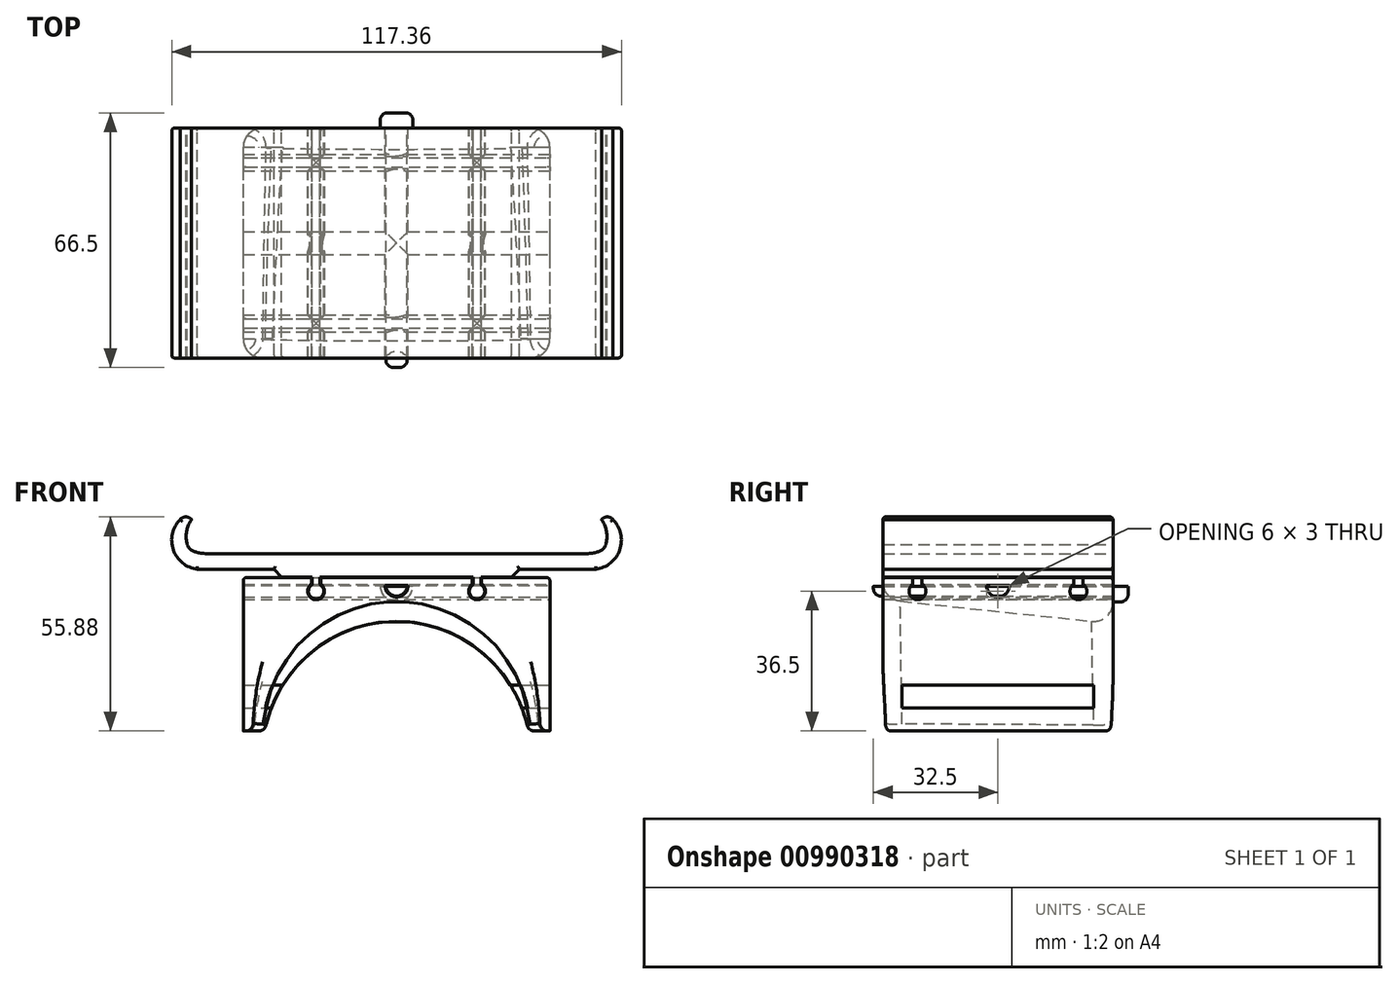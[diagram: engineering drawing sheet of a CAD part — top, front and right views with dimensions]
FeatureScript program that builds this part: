
annotation { "Feature Type Name" : "Feature", "Feature Type Description" : "" }
export const myFeature = defineFeature(function(context is Context, id is Id, definition is map)
    precondition{}
    {
        {
            var Q0;
            Q0=qCreatedBy(makeId("Front.planeOp"),FACE);
            var sketch = newSketch(context, id + "F0", { "sketchPlane" : qUnion([Q0])});
            skLineSegment(sketch, "E0", {"start": v(-53.5, 0) * mm, "end": v(53.5, 0) * mm, "construction": true});
            skLineSegment(sketch, "E1", {"start": v(-46.57, -9) * mm, "end": v(46.57, -9) * mm});
            skLineSegment(sketch, "E2", {"start": v(0, 0) * mm, "end": v(0, -9) * mm, "construction": true});
            skLineSegment(sketch, "E3", {"start": v(0, -4.5) * mm, "end": v(54.9, -4.5) * mm, "construction": true});
            skArc(sketch, "E4", {"start": v(54.63, -6.57) * mm, "mid": v(54.79, -3.16) * mm, "end": v(53.5, 0) * mm});
            skFitSpline(sketch, "E5", {"points": [v(54.63, -6.57) * mm, v(52.6, -8.42) * mm, v(46.57, -9) * mm], "startDerivative": vector(-3.86, -8.9) * mm, "endDerivative": vector(-15.68, 0) * mm});
            skPoint(sketch, "E6.orphan", {"position": v(53.5, -9) * mm});
            skArc(sketch, "E7.MirrorCS", {"start": v(-54.63, -6.57) * mm, "mid": v(-54.79, -3.16) * mm, "end": v(-53.5, 0) * mm});
            skFitSpline(sketch, "E8.MirrorCS", {"points": [v(-54.63, -6.57) * mm, v(-52.6, -8.42) * mm, v(-46.57, -9) * mm], "startDerivative": vector(3.86, -8.9) * mm, "endDerivative": vector(15.68, 0) * mm});
            skPoint(sketch, "E9.orphan", {"position": v(-53.5, -9) * mm});
            skLineSegment(sketch, "E10", {"start": v(-52, -13) * mm, "end": v(-32, -13) * mm});
            skArc(sketch, "E11", {"start": v(56.5, 0) * mm, "mid": v(55, 0.68) * mm, "end": v(53.5, 0) * mm});
            skArc(sketch, "E12", {"start": v(52, -13) * mm, "mid": v(58.26, -7.89) * mm, "end": v(56.5, 0) * mm});
            skLineSegment(sketch, "E13.MirrorCS", {"start": v(0, -4.5) * mm, "end": v(-54.9, -4.5) * mm, "construction": true});
            skLineSegment(sketch, "E14.MirrorCS", {"start": v(53.5, 0) * mm, "end": v(-53.5, 0) * mm, "construction": true});
            skArc(sketch, "E15.MirrorCS", {"start": v(-52, -13) * mm, "mid": v(-58.26, -7.89) * mm, "end": v(-56.5, 0) * mm});
            skArc(sketch, "E16.MirrorCS", {"start": v(-56.5, 0) * mm, "mid": v(-55, 0.68) * mm, "end": v(-53.5, 0) * mm});
            skLineSegment(sketch, "E17", {"start": v(30, -15) * mm, "end": v(32, -13) * mm});
            skLineSegment(sketch, "E18.trimOffspring", {"start": v(32, -13) * mm, "end": v(52, -13) * mm});
            skLineSegment(sketch, "E19", {"start": v(0, -15) * mm, "end": v(20, -15) * mm});
            skLineSegment(sketch, "E20.MirrorCS", {"start": v(-30, -15) * mm, "end": v(-32, -13) * mm});
            skLineSegment(sketch, "E21.MirrorCS", {"start": v(0, -15) * mm, "end": v(-20, -15) * mm});
            skLineSegment(sketch, "E22", {"start": v(20, -15) * mm, "end": v(20, -17) * mm});
            skLineSegment(sketch, "E23", {"start": v(22, -17) * mm, "end": v(22, -15) * mm});
            skLineSegment(sketch, "E24.trimOffspring", {"start": v(22, -15) * mm, "end": v(30, -15) * mm});
            skArc(sketch, "E25", {"start": v(20, -17) * mm, "mid": v(21, -20.73) * mm, "end": v(22, -17) * mm});
            skLineSegment(sketch, "E26.MirrorCS", {"start": v(-20, -15) * mm, "end": v(-20, -17) * mm});
            skArc(sketch, "E27.MirrorCS", {"start": v(-20, -17) * mm, "mid": v(-21, -20.73) * mm, "end": v(-22, -17) * mm});
            skLineSegment(sketch, "E28.MirrorCS", {"start": v(-22, -17) * mm, "end": v(-22, -15) * mm});
            skLineSegment(sketch, "E29.trimOffspring", {"start": v(-22, -15) * mm, "end": v(-30, -15) * mm});
            skSolve(sketch);
        }
        {
            var Q0;
            Q0=makeQuery(id+"F0.imprint","IMPRINT",FACE,{"disambiguationData":[TD([[makeQuery(id+"F0.imprint","IMPRINT",EDGE,{"derivedFrom":sQuery(id+"F0.wireOp",EDGE,"E1")}),-1.0]])]});
            extrude(context, id + "F1", {"entities" : qUnion([Q0]), "depth" : 60 * mm, "offsetDistance" : 25 * mm});
        }
        {
            var Q0;
            Q0=qCreatedBy(makeId("Front.planeOp"),FACE);
            var sketch = newSketch(context, id + "F2", { "sketchPlane" : qUnion([Q0])});
            skLineSegment(sketch, "E30.0", {"start": v(-22.2, -15.2) * mm, "end": v(-30, -15.2) * mm});
            skLineSegment(sketch, "E30.1", {"start": v(-22.2, -16.89) * mm, "end": v(-22.2, -15.2) * mm});
            skArc(sketch, "E30.2", {"start": v(-19.8, -16.89) * mm, "mid": v(-21, -20.93) * mm, "end": v(-22.2, -16.89) * mm});
            skLineSegment(sketch, "E30.3", {"start": v(-19.8, -15.2) * mm, "end": v(-19.8, -16.89) * mm});
            skLineSegment(sketch, "E30.4", {"start": v(19.8, -15.2) * mm, "end": v(-19.8, -15.2) * mm});
            skLineSegment(sketch, "E30.5", {"start": v(22.2, -15.2) * mm, "end": v(30, -15.2) * mm});
            skLineSegment(sketch, "E30.6", {"start": v(22.2, -16.89) * mm, "end": v(22.2, -15.2) * mm});
            skArc(sketch, "E30.7", {"start": v(19.8, -16.89) * mm, "mid": v(21, -20.93) * mm, "end": v(22.2, -16.89) * mm});
            skLineSegment(sketch, "E30.8", {"start": v(19.8, -15.2) * mm, "end": v(19.8, -16.89) * mm});
            skLineSegment(sketch, "E31", {"start": v(0, 0) * mm, "end": v(0, -23.2) * mm, "construction": true});
            skLineSegment(sketch, "E32", {"start": v(30, -15.2) * mm, "end": v(40, -15.2) * mm});
            skLineSegment(sketch, "E33", {"start": v(40, -15.2) * mm, "end": v(40, -55.2) * mm});
            skLineSegment(sketch, "E34", {"start": v(40, -55.2) * mm, "end": v(0, -55.2) * mm});
            skLineSegment(sketch, "E35.MirrorCS", {"start": v(-30, -15.2) * mm, "end": v(-40, -15.2) * mm});
            skLineSegment(sketch, "E36.MirrorCS", {"start": v(-40, -15.2) * mm, "end": v(-40, -55.2) * mm});
            skLineSegment(sketch, "E37.MirrorCS", {"start": v(-40, -55.2) * mm, "end": v(0, -55.2) * mm});
            skLineSegment(sketch, "E38", {"start": v(0, -17.2) * mm, "end": v(3, -17.2) * mm});
            skArc(sketch, "E39", {"start": v(0, -20.2) * mm, "mid": v(2.12, -19.32) * mm, "end": v(3, -17.2) * mm});
            skLineSegment(sketch, "E40.MirrorCS", {"start": v(0, -17.2) * mm, "end": v(-3, -17.2) * mm});
            skArc(sketch, "E41.MirrorCS", {"start": v(0, -20.2) * mm, "mid": v(-2.12, -19.32) * mm, "end": v(-3, -17.2) * mm});
            skSolve(sketch);
        }
        {
            var Q0;
            Q0 = qSketchRegion(id + "F2", true);
            extrude(context, id + "F3", {"entities" : qUnion([Q0]), "depth" : 60 * mm, "offsetDistance" : 25 * mm});
        }
        {
            var Q0;
            Q0=makeQuery(id+"F3.opExtrude","CAP_EDGE",EDGE,{"disambiguationData":[OSD([sQuery(id+"F2.wireOp",EDGE,"E30.4")])],"isStart":true});
            cPlane(context, id + "F4", {"entities" : qUnion([Q0]), "cplaneType" : CPlaneType.LINE_ANGLE, "offset" : 25 * mm, "angle" : 6 * degree, "width" : 150 * mm, "height" : 150 * mm});
        }
        {
            var Q0;
            Q0=qCreatedBy(id+"F4.planeOp",FACE);
            var sketch = newSketch(context, id + "F5", { "sketchPlane" : qUnion([Q0])});
            skArc(sketch, "E42", {"start": v(35, -62) * mm, "mid": v(0, -27) * mm, "end": v(-35, -62) * mm});
            skLineSegment(sketch, "E43", {"start": v(35, -62) * mm, "end": v(-35, -62) * mm});
            skSolve(sketch);
        }
        {
            var Q0;
            Q0 = qSketchRegion(id + "F5", true);
            extrude(context, id + "F6", {"entities" : qUnion([Q0]), "operationType" : NewBodyOperationType.REMOVE, "endBound" : BoundingType.SYMMETRIC, "depth" : 193.8 * mm, "offsetDistance" : 25 * mm});
        }
        {
            var Q0;
            Q0=qCreatedBy(makeId("Right.planeOp"),FACE);
            var sketch = newSketch(context, id + "F7", { "sketchPlane" : qUnion([Q0])});
            skLineSegment(sketch, "E44.4", {"start": v(-10.2, -15.2) * mm, "end": v(-30, -15.2) * mm, "construction": true});
            skLineSegment(sketch, "E44.6", {"start": v(-7.8, -16.89) * mm, "end": v(-7.8, -15.2) * mm});
            skArc(sketch, "E44.7", {"start": v(-10.2, -16.89) * mm, "mid": v(-9, -20.93) * mm, "end": v(-7.8, -16.89) * mm});
            skLineSegment(sketch, "E44.8", {"start": v(-10.2, -15.2) * mm, "end": v(-10.2, -16.89) * mm});
            skLineSegment(sketch, "E45", {"start": v(-30, -3.72) * mm, "end": v(-30, -26.92) * mm, "construction": true});
            skLineSegment(sketch, "E46", {"start": v(-30, -17.2) * mm, "end": v(-27, -17.2) * mm});
            skArc(sketch, "E47", {"start": v(-30, -20.2) * mm, "mid": v(-27.88, -19.32) * mm, "end": v(-27, -17.2) * mm});
            skPoint(sketch, "E48.MirrorCS.start.orphan", {"position": v(-28.4, -23.92) * mm});
            skLineSegment(sketch, "E49.MirrorCS", {"start": v(-30, -17.2) * mm, "end": v(-33, -17.2) * mm});
            skArc(sketch, "E50.MirrorCS", {"start": v(-30, -20.2) * mm, "mid": v(-32.12, -19.32) * mm, "end": v(-33, -17.2) * mm});
            skLineSegment(sketch, "E51.MirrorCS", {"start": v(-49.8, -15.2) * mm, "end": v(-30, -15.2) * mm, "construction": true});
            skLineSegment(sketch, "E52.MirrorCS", {"start": v(-49.8, -15.2) * mm, "end": v(-49.8, -16.89) * mm});
            skArc(sketch, "E53.MirrorCS", {"start": v(-49.8, -16.89) * mm, "mid": v(-51, -20.93) * mm, "end": v(-52.2, -16.89) * mm});
            skLineSegment(sketch, "E54.MirrorCS", {"start": v(-52.2, -16.89) * mm, "end": v(-52.2, -15.2) * mm});
            skPoint(sketch, "E55.MirrorCS.start.orphan", {"position": v(-52.2, -15.2) * mm});
            skPoint(sketch, "E56.0", {"position": v(-30, -15.2) * mm});
            skLineSegment(sketch, "E57", {"start": v(-7.8, -15.2) * mm, "end": v(-10.2, -15.2) * mm});
            skLineSegment(sketch, "E58.MirrorCS", {"start": v(-52.2, -15.2) * mm, "end": v(-49.8, -15.2) * mm});
            skLineSegment(sketch, "E59", {"start": v(-30, -43.2) * mm, "end": v(-5, -43.2) * mm});
            skLineSegment(sketch, "E60", {"start": v(-5, -43.2) * mm, "end": v(-5, -49.2) * mm});
            skLineSegment(sketch, "E61", {"start": v(-5, -49.2) * mm, "end": v(-30, -49.2) * mm});
            skLineSegment(sketch, "E62.MirrorCS", {"start": v(-30, -43.2) * mm, "end": v(-55, -43.2) * mm});
            skLineSegment(sketch, "E63.MirrorCS", {"start": v(-55, -43.2) * mm, "end": v(-55, -49.2) * mm});
            skLineSegment(sketch, "E64.MirrorCS", {"start": v(-55, -49.2) * mm, "end": v(-30, -49.2) * mm});
            skSolve(sketch);
        }
        {
            var Q0;
            Q0 = qSketchRegion(id + "F7", true);
            extrude(context, id + "F8", {"entities" : qUnion([Q0]), "operationType" : NewBodyOperationType.REMOVE, "endBound" : BoundingType.SYMMETRIC, "oppositeDirection" : true, "depth" : 100 * mm, "offsetDistance" : 25 * mm});
        }
        {
            var Q0;
            Q0=makeQuery(id+"F1.opExtrude","CAP_EDGE",EDGE,{"disambiguationData":[OSD([sQuery(id+"F0.wireOp",EDGE,"E12")])],"isStart":false});
            var Q1;
            Q1=makeQuery(id+"F1.opExtrude","CAP_EDGE",EDGE,{"disambiguationData":[OSD([sQuery(id+"F0.wireOp",EDGE,"E18.trimOffspring")])],"isStart":false});
            var Q2;
            Q2=makeQuery(id+"F1.opExtrude","CAP_EDGE",EDGE,{"disambiguationData":[OSD([sQuery(id+"F0.wireOp",EDGE,"E17")])],"isStart":false});
            var Q3;
            Q3=makeQuery(id+"F1.opExtrude","CAP_EDGE",EDGE,{"disambiguationData":[OSD([sQuery(id+"F0.wireOp",EDGE,"E11")])],"isStart":false});
            var Q4;
            Q4=makeQuery(id+"F1.opExtrude","CAP_EDGE",EDGE,{"disambiguationData":[OSD([sQuery(id+"F0.wireOp",EDGE,"E17")])],"isStart":true});
            var Q5;
            Q5=makeQuery(id+"F1.opExtrude","CAP_EDGE",EDGE,{"disambiguationData":[OSD([sQuery(id+"F0.wireOp",EDGE,"E18.trimOffspring")])],"isStart":true});
            var Q6;
            Q6=makeQuery(id+"F1.opExtrude","CAP_EDGE",EDGE,{"disambiguationData":[OSD([sQuery(id+"F0.wireOp",EDGE,"E12")])],"isStart":true});
            var Q7;
            Q7=makeQuery(id+"F1.opExtrude","CAP_EDGE",EDGE,{"disambiguationData":[OSD([sQuery(id+"F0.wireOp",EDGE,"E11")])],"isStart":true});
            var Q8;
            Q8=makeQuery(id+"F1.opExtrude","CAP_EDGE",EDGE,{"disambiguationData":[OSD([sQuery(id+"F0.wireOp",EDGE,"E20.MirrorCS")])],"isStart":true});
            var Q9;
            Q9=makeQuery(id+"F1.opExtrude","CAP_EDGE",EDGE,{"disambiguationData":[OSD([sQuery(id+"F0.wireOp",EDGE,"E10")])],"isStart":true});
            var Q10;
            Q10=makeQuery(id+"F1.opExtrude","CAP_EDGE",EDGE,{"disambiguationData":[OSD([sQuery(id+"F0.wireOp",EDGE,"E15.MirrorCS")])],"isStart":true});
            var Q11;
            Q11=makeQuery(id+"F1.opExtrude","CAP_EDGE",EDGE,{"disambiguationData":[OSD([sQuery(id+"F0.wireOp",EDGE,"E16.MirrorCS")])],"isStart":true});
            var Q12;
            Q12=makeQuery(id+"F1.opExtrude","CAP_EDGE",EDGE,{"disambiguationData":[OSD([sQuery(id+"F0.wireOp",EDGE,"E20.MirrorCS")])],"isStart":false});
            var Q13;
            Q13=makeQuery(id+"F1.opExtrude","CAP_EDGE",EDGE,{"disambiguationData":[OSD([sQuery(id+"F0.wireOp",EDGE,"E10")])],"isStart":false});
            var Q14;
            Q14=makeQuery(id+"F1.opExtrude","CAP_EDGE",EDGE,{"disambiguationData":[OSD([sQuery(id+"F0.wireOp",EDGE,"E15.MirrorCS")])],"isStart":false});
            var Q15;
            Q15=makeQuery(id+"F1.opExtrude","CAP_EDGE",EDGE,{"disambiguationData":[OSD([sQuery(id+"F0.wireOp",EDGE,"E16.MirrorCS")])],"isStart":false});
            var Q16;
            Q16=makeQuery(id+"F3.opExtrude","CAP_EDGE",EDGE,{"disambiguationData":[OSD([sQuery(id+"F2.wireOp",EDGE,"E30.0"),sQuery(id+"F2.wireOp",EDGE,"E35.MirrorCS")])],"isStart":false});
            var Q17;
            {var subQ0=sQuery(id+"F2.wireOp",EDGE,"E36.MirrorCS");var subQ1=sQuery(id+"F2.wireOp",EDGE,"E35.MirrorCS");Q17=makeQuery(id+"F8.boolean.opBoolean","SPLIT",EDGE,{"disambiguationData":[TD([makeQuery(id+"F8.opExtrude","SWEPT_FACE",FACE,{"disambiguationData":[OSD([sQuery(id+"F7.wireOp",EDGE,"E54.MirrorCS")])]})])],"derivedFrom":makeQuery(id+"F3.opExtrude","SWEPT_EDGE",EDGE,{"disambiguationData":[OSD([subQ1,subQ0])]})});}
            var Q18;
            {var subQ0=sQuery(id+"F2.wireOp",EDGE,"E35.MirrorCS");var subQ1=sQuery(id+"F2.wireOp",EDGE,"E36.MirrorCS");Q18=makeQuery(id+"F8.boolean.opBoolean","SPLIT",EDGE,{"disambiguationData":[TD([makeQuery(id+"F8.opExtrude","SWEPT_FACE",FACE,{"disambiguationData":[OSD([sQuery(id+"F7.wireOp",EDGE,"E44.8")])]})])],"derivedFrom":makeQuery(id+"F3.opExtrude","SWEPT_EDGE",EDGE,{"disambiguationData":[OSD([subQ0,subQ1])]})});}
            var Q19;
            {var subQ0=sQuery(id+"F2.wireOp",EDGE,"E36.MirrorCS");var subQ1=sQuery(id+"F2.wireOp",EDGE,"E35.MirrorCS");Q19=makeQuery(id+"F8.boolean.opBoolean","SPLIT",EDGE,{"disambiguationData":[TD([makeQuery(id+"F8.opExtrude","SWEPT_FACE",FACE,{"disambiguationData":[OSD([sQuery(id+"F7.wireOp",EDGE,"E44.6")])]})])],"derivedFrom":makeQuery(id+"F3.opExtrude","SWEPT_EDGE",EDGE,{"disambiguationData":[OSD([subQ1,subQ0])]})});}
            var Q20;
            Q20=makeQuery(id+"F3.opExtrude","CAP_EDGE",EDGE,{"disambiguationData":[OSD([sQuery(id+"F2.wireOp",EDGE,"E30.0"),sQuery(id+"F2.wireOp",EDGE,"E35.MirrorCS")])],"isStart":true});
            var Q21;
            Q21=makeQuery(id+"F3.opExtrude","CAP_EDGE",EDGE,{"disambiguationData":[OSD([sQuery(id+"F2.wireOp",EDGE,"E30.4")])],"isStart":true});
            var Q22;
            Q22=makeQuery(id+"F3.opExtrude","CAP_EDGE",EDGE,{"disambiguationData":[OSD([sQuery(id+"F2.wireOp",EDGE,"E30.5"),sQuery(id+"F2.wireOp",EDGE,"E32")])],"isStart":true});
            var Q23;
            {var subQ0=sQuery(id+"F2.wireOp",EDGE,"E33");var subQ1=sQuery(id+"F2.wireOp",EDGE,"E32");Q23=makeQuery(id+"F8.boolean.opBoolean","SPLIT",EDGE,{"disambiguationData":[TD([makeQuery(id+"F8.opExtrude","SWEPT_FACE",FACE,{"disambiguationData":[OSD([sQuery(id+"F7.wireOp",EDGE,"E44.6")])]})])],"derivedFrom":makeQuery(id+"F3.opExtrude","SWEPT_EDGE",EDGE,{"disambiguationData":[OSD([subQ1,subQ0])]})});}
            var Q24;
            {var subQ0=sQuery(id+"F2.wireOp",EDGE,"E32");var subQ1=sQuery(id+"F2.wireOp",EDGE,"E33");Q24=makeQuery(id+"F8.boolean.opBoolean","SPLIT",EDGE,{"disambiguationData":[TD([makeQuery(id+"F8.opExtrude","SWEPT_FACE",FACE,{"disambiguationData":[OSD([sQuery(id+"F7.wireOp",EDGE,"E44.8")])]})])],"derivedFrom":makeQuery(id+"F3.opExtrude","SWEPT_EDGE",EDGE,{"disambiguationData":[OSD([subQ0,subQ1])]})});}
            var Q25;
            {var subQ0=sQuery(id+"F2.wireOp",EDGE,"E33");var subQ1=sQuery(id+"F2.wireOp",EDGE,"E32");Q25=makeQuery(id+"F8.boolean.opBoolean","SPLIT",EDGE,{"disambiguationData":[TD([makeQuery(id+"F8.opExtrude","SWEPT_FACE",FACE,{"disambiguationData":[OSD([sQuery(id+"F7.wireOp",EDGE,"E54.MirrorCS")])]})])],"derivedFrom":makeQuery(id+"F3.opExtrude","SWEPT_EDGE",EDGE,{"disambiguationData":[OSD([subQ1,subQ0])]})});}
            var Q26;
            Q26=makeQuery(id+"F3.opExtrude","CAP_EDGE",EDGE,{"disambiguationData":[OSD([sQuery(id+"F2.wireOp",EDGE,"E30.5"),sQuery(id+"F2.wireOp",EDGE,"E32")])],"isStart":false});
            var Q27;
            Q27=makeQuery(id+"F3.opExtrude","CAP_EDGE",EDGE,{"disambiguationData":[OSD([sQuery(id+"F2.wireOp",EDGE,"E30.4")])],"isStart":false});
            fillet(context, id + "F9", {"entities" : qUnion([Q0, Q1, Q2, Q3, Q4, Q5, Q6, Q7, Q8, Q9, Q10, Q11, Q12, Q13, Q14, Q15, Q16, Q17, Q18, Q19, Q20, Q21, Q22, Q23, Q24, Q25, Q26, Q27]), "radius" : .7 * mm, "tangentPropagation" : true, "allowEdgeOverflow" : false});
        }
        {
            var Q0;
            Q0=makeQuery(id+"F3.opExtrude","CAP_EDGE",EDGE,{"disambiguationData":[OSD([sQuery(id+"F2.wireOp",EDGE,"E33")])],"isStart":false});
            var Q1;
            Q1=makeQuery(id+"F3.opExtrude","CAP_EDGE",EDGE,{"disambiguationData":[OSD([sQuery(id+"F2.wireOp",EDGE,"E33")])],"isStart":true});
            var Q2;
            Q2=makeQuery(id+"F3.opExtrude","CAP_EDGE",EDGE,{"disambiguationData":[OSD([sQuery(id+"F2.wireOp",EDGE,"E36.MirrorCS")])],"isStart":false});
            var Q3;
            Q3=makeQuery(id+"F3.opExtrude","CAP_EDGE",EDGE,{"disambiguationData":[OSD([sQuery(id+"F2.wireOp",EDGE,"E36.MirrorCS")])],"isStart":true});
            fillet(context, id + "F10", {"entities" : qUnion([Q0, Q1, Q2, Q3]), "radius" : 5 * mm, "tangentPropagation" : true, "allowEdgeOverflow" : false});
        }
        {
            var Q0;
            Q0=makeQuery(id+"F6.boolean.opBoolean","INTERSECT",EDGE,{"derivedFrom":[makeQuery(id+"F3.opExtrude","CAP_FACE",FACE,{"disambiguationData":[OSD([sQuery(id+"F2.wireOp",EDGE,"E30.0"),sQuery(id+"F2.wireOp",EDGE,"E30.1"),sQuery(id+"F2.wireOp",EDGE,"E30.2"),sQuery(id+"F2.wireOp",EDGE,"E30.3"),sQuery(id+"F2.wireOp",EDGE,"E30.4"),sQuery(id+"F2.wireOp",EDGE,"E30.5"),sQuery(id+"F2.wireOp",EDGE,"E30.6"),sQuery(id+"F2.wireOp",EDGE,"E30.7"),sQuery(id+"F2.wireOp",EDGE,"E30.8"),sQuery(id+"F2.wireOp",EDGE,"E32"),sQuery(id+"F2.wireOp",EDGE,"E33"),sQuery(id+"F2.wireOp",EDGE,"E34"),sQuery(id+"F2.wireOp",EDGE,"E35.MirrorCS"),sQuery(id+"F2.wireOp",EDGE,"E36.MirrorCS"),sQuery(id+"F2.wireOp",EDGE,"E37.MirrorCS"),sQuery(id+"F2.wireOp",EDGE,"E38"),sQuery(id+"F2.wireOp",EDGE,"E39"),sQuery(id+"F2.wireOp",EDGE,"E40.MirrorCS"),sQuery(id+"F2.wireOp",EDGE,"E41.MirrorCS")])],"isStart":true}),makeQuery(id+"F6.opExtrude","SWEPT_FACE",FACE,{"disambiguationData":[OSD([sQuery(id+"F5.wireOp",EDGE,"E42")])]})]});
            var Q1;
            Q1=makeQuery(id+"F6.boolean.opBoolean","INTERSECT",EDGE,{"derivedFrom":[makeQuery(id+"F3.opExtrude","CAP_FACE",FACE,{"disambiguationData":[OSD([sQuery(id+"F2.wireOp",EDGE,"E30.0"),sQuery(id+"F2.wireOp",EDGE,"E30.1"),sQuery(id+"F2.wireOp",EDGE,"E30.2"),sQuery(id+"F2.wireOp",EDGE,"E30.3"),sQuery(id+"F2.wireOp",EDGE,"E30.4"),sQuery(id+"F2.wireOp",EDGE,"E30.5"),sQuery(id+"F2.wireOp",EDGE,"E30.6"),sQuery(id+"F2.wireOp",EDGE,"E30.7"),sQuery(id+"F2.wireOp",EDGE,"E30.8"),sQuery(id+"F2.wireOp",EDGE,"E32"),sQuery(id+"F2.wireOp",EDGE,"E33"),sQuery(id+"F2.wireOp",EDGE,"E34"),sQuery(id+"F2.wireOp",EDGE,"E35.MirrorCS"),sQuery(id+"F2.wireOp",EDGE,"E36.MirrorCS"),sQuery(id+"F2.wireOp",EDGE,"E37.MirrorCS"),sQuery(id+"F2.wireOp",EDGE,"E38"),sQuery(id+"F2.wireOp",EDGE,"E39"),sQuery(id+"F2.wireOp",EDGE,"E40.MirrorCS"),sQuery(id+"F2.wireOp",EDGE,"E41.MirrorCS")])],"isStart":false}),makeQuery(id+"F6.opExtrude","SWEPT_FACE",FACE,{"disambiguationData":[OSD([sQuery(id+"F5.wireOp",EDGE,"E42")])]})]});
            fillet(context, id + "F11", {"entities" : qUnion([Q0, Q1]), "radius" : 5 * mm, "tangentPropagation" : true, "allowEdgeOverflow" : false});
        }
        {
            var Q0;
            Q0=makeQuery(id+"F6.boolean.opBoolean","INTERSECT",EDGE,{"disambiguationData":[OD(0.0)],"derivedFrom":[makeQuery(id+"F3.opExtrude","SWEPT_FACE",FACE,{"disambiguationData":[OSD([sQuery(id+"F2.wireOp",EDGE,"E34"),sQuery(id+"F2.wireOp",EDGE,"E37.MirrorCS")])]}),makeQuery(id+"F6.opExtrude","SWEPT_FACE",FACE,{"disambiguationData":[OSD([sQuery(id+"F5.wireOp",EDGE,"E42")])]})]});
            var Q1;
            Q1=makeQuery(id+"F6.boolean.opBoolean","INTERSECT",EDGE,{"disambiguationData":[OD(1.0)],"derivedFrom":[makeQuery(id+"F3.opExtrude","SWEPT_FACE",FACE,{"disambiguationData":[OSD([sQuery(id+"F2.wireOp",EDGE,"E34"),sQuery(id+"F2.wireOp",EDGE,"E37.MirrorCS")])]}),makeQuery(id+"F6.opExtrude","SWEPT_FACE",FACE,{"disambiguationData":[OSD([sQuery(id+"F5.wireOp",EDGE,"E42")])]})]});
            fillet(context, id + "F12", {"entities" : qUnion([Q0, Q1]), "radius" : 2 * mm, "tangentPropagation" : true, "allowEdgeOverflow" : false});
        }
        {
            var Q0;
            Q0=qCreatedBy(makeId("Front.planeOp"),FACE);
            var sketch = newSketch(context, id + "F13", { "sketchPlane" : qUnion([Q0])});
            skArc(sketch, "E65.0", {"start": v(-2.8, -17.4) * mm, "mid": v(0, -20) * mm, "end": v(2.8, -17.4) * mm});
            skLineSegment(sketch, "E65.1", {"start": v(2.8, -17.4) * mm, "end": v(-2.8, -17.4) * mm});
            skSolve(sketch);
        }
        {
            var Q0;
            Q0 = qSketchRegion(id + "F13", true);
            extrude(context, id + "F14", {"entities" : qUnion([Q0]), "depth" : 62.5 * mm, "offsetDistance" : 25 * mm});
        }
        {
            var Q0;
            Q0=makeQuery(id+"F14.opExtrude","CAP_EDGE",EDGE,{"disambiguationData":[OSD([sQuery(id+"F13.wireOp",EDGE,"E65.0")])],"isStart":false});
            fillet(context, id + "F15", {"entities" : qUnion([Q0]), "radius" : 2 * mm, "tangentPropagation" : true, "allowEdgeOverflow" : false});
        }
        {
            var Q0;
            Q0=makeQuery(id+"F14.opExtrude","CAP_FACE",FACE,{"disambiguationData":[OSD([sQuery(id+"F13.wireOp",EDGE,"E65.0"),sQuery(id+"F13.wireOp",EDGE,"E65.1")])],"isStart":true});
            var sketch = newSketch(context, id + "F16", { "sketchPlane" : qUnion([Q0])});
            skArc(sketch, "E66.0", {"start": v(4.3, -17.4) * mm, "mid": v(0, -21.5) * mm, "end": v(-4.3, -17.4) * mm});
            skPoint(sketch, "E67", {"position": v(0, -17.4) * mm});
            skLineSegment(sketch, "E68", {"start": v(-4.3, -17.4) * mm, "end": v(4.3, -17.4) * mm});
            skSolve(sketch);
        }
        {
            var Q0;
            Q0 = qSketchRegion(id + "F16", true);
            extrude(context, id + "F17", {"entities" : qUnion([Q0]), "operationType" : NewBodyOperationType.ADD, "depth" : 4 * mm, "offsetDistance" : 25 * mm});
        }
        {
            var Q0;
            Q0=makeQuery(id+"F17.opExtrude","CAP_EDGE",EDGE,{"disambiguationData":[OSD([sQuery(id+"F16.wireOp",EDGE,"E66.0")])],"isStart":false});
            var Q1;
            Q1=makeQuery(id+"F17.opExtrude","CAP_EDGE",EDGE,{"disambiguationData":[OSD([sQuery(id+"F16.wireOp",EDGE,"E66.0")])],"isStart":true});
            fillet(context, id + "F18", {"entities" : qUnion([Q0, Q1]), "radius" : 2 * mm, "tangentPropagation" : true, "allowEdgeOverflow" : false});
        }
    });
